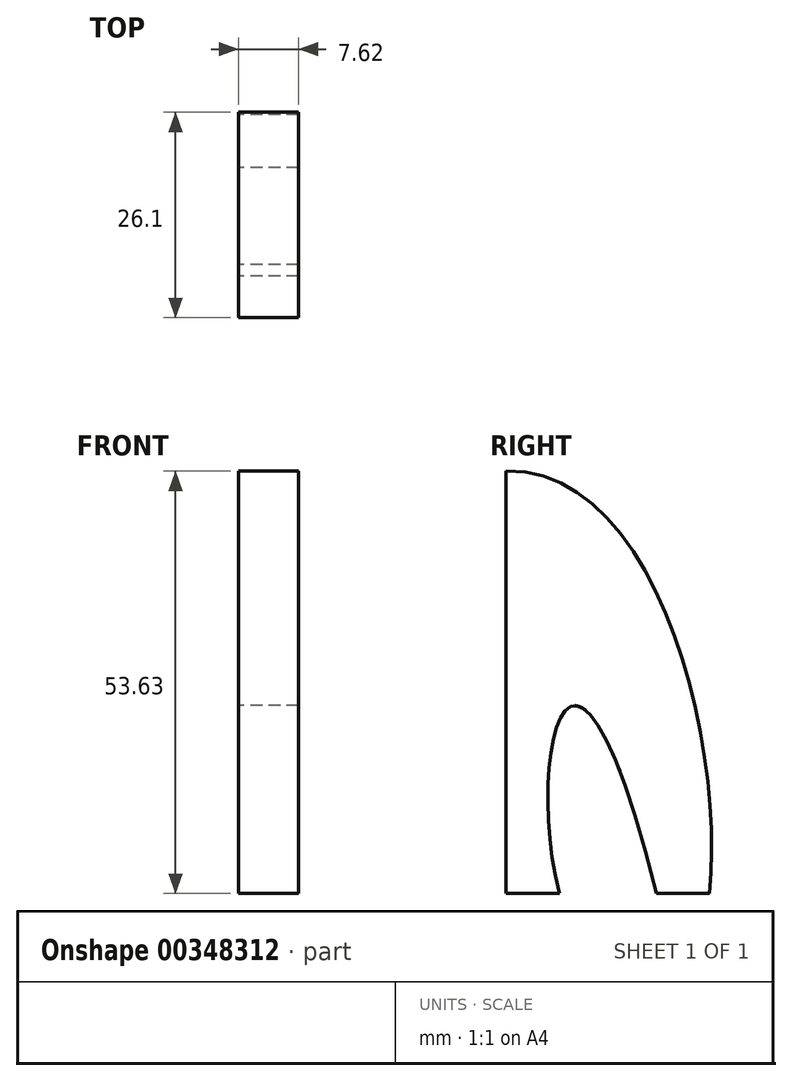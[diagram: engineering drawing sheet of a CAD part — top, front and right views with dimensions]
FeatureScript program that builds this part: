
annotation { "Feature Type Name" : "Feature", "Feature Type Description" : "" }
export const myFeature = defineFeature(function(context is Context, id is Id, definition is map)
    precondition{}
    {
        {
            var Q0;
            Q0=qCreatedBy(makeId("Right.planeOp"),FACE);
            var sketch = newSketch(context, id + "F0", { "sketchPlane" : qUnion([Q0])});
            skLineSegment(sketch, "E0", {"start": v(-19.1, 13.2) * mm, "end": v(-19.1, -40.43) * mm});
            skLineSegment(sketch, "E1", {"start": v(-19.1, -40.43) * mm, "end": v(6.74, -40.43) * mm});
            skFitSpline(sketch, "E2", {"points": [v(-19.1, 13.2) * mm, v(6.74, -40.43) * mm], "startDerivative": vector(57.27, 1.68) * mm, "endDerivative": vector(-5.9, -57.27) * mm});
            skFitSpline(sketch, "E3", {"points": [v(-12.35, -40.43) * mm, v(0, -40.43) * mm], "startDerivative": vector(-13, 50.37) * mm, "endDerivative": vector(32.8, -131.96) * mm});
            skSolve(sketch);
        }
        {
            var Q0;
            {var subQ3=sQuery(id+"F0.wireOp",EDGE,"E0");Q0=makeQuery(id+"F0.imprint","IMPRINT",FACE,{"disambiguationData":[TD([[makeQuery(id+"F0.imprint","IMPRINT",EDGE,{"derivedFrom":subQ3}),1.0]])]});}
            extrude(context, id + "F1", {"entities" : qUnion([Q0]), "depth" : 7.62 * mm});
        }
    });
